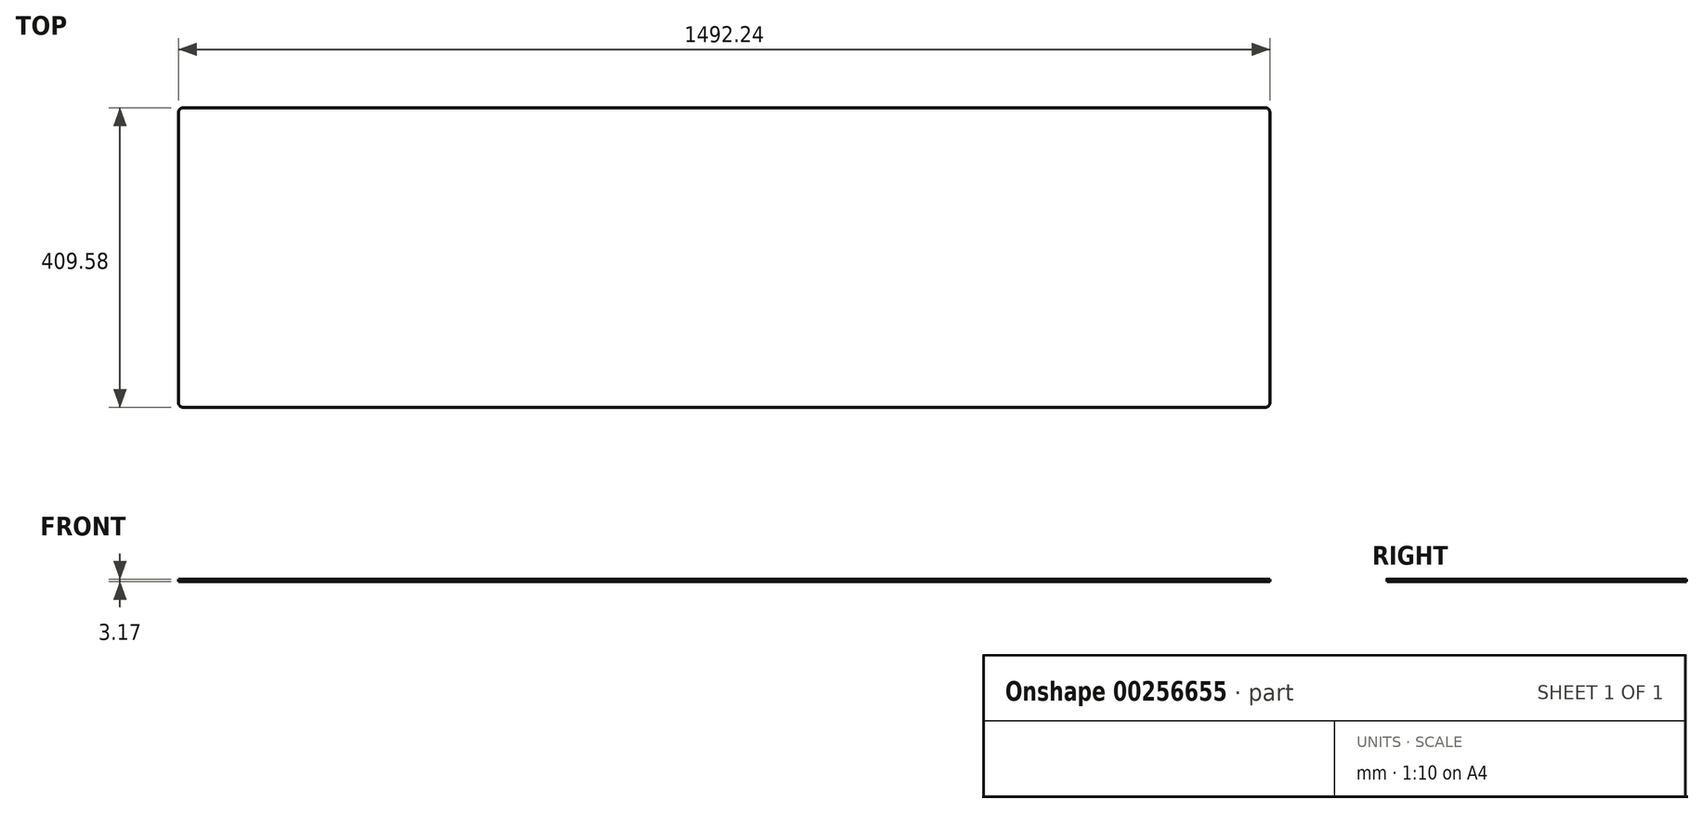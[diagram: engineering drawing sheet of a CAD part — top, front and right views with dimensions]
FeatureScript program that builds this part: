
annotation { "Feature Type Name" : "Feature", "Feature Type Description" : "" }
export const myFeature = defineFeature(function(context is Context, id is Id, definition is map)
    precondition{}
    {
        {
            var Q0;
            Q0=qCreatedBy(makeId("Top.planeOp"),FACE);
            var sketch = newSketch(context, id + "F0", { "sketchPlane" : qUnion([Q0])});
            skLineSegment(sketch, "E0.bottom", {"start": v(739.77, 204.79) * mm, "end": v(-739.78, 204.79) * mm});
            skLineSegment(sketch, "E0.top", {"start": v(739.78, -204.79) * mm, "end": v(-739.78, -204.79) * mm});
            skLineSegment(sketch, "E0.left", {"start": v(746.12, 198.44) * mm, "end": v(746.12, -198.44) * mm});
            skLineSegment(sketch, "E0.right", {"start": v(-746.12, 198.44) * mm, "end": v(-746.12, -198.44) * mm});
            skPoint(sketch, "E0.middle", {"position": v(0, 0) * mm});
            skPoint(sketch, "E1.visualSharp", {"position": v(746.12, -204.79) * mm});
            skArc(sketch, "E1.filletArc", {"start": v(739.78, -204.79) * mm, "mid": v(744.27, -202.93) * mm, "end": v(746.13, -198.44) * mm});
            skPoint(sketch, "E2.visualSharp", {"position": v(-746.12, -204.79) * mm});
            skArc(sketch, "E2.filletArc", {"start": v(-746.12, -198.44) * mm, "mid": v(-744.27, -202.93) * mm, "end": v(-739.78, -204.79) * mm});
            skPoint(sketch, "E3.visualSharp", {"position": v(746.12, 204.79) * mm});
            skArc(sketch, "E3.filletArc", {"start": v(746.12, 198.44) * mm, "mid": v(744.27, 202.93) * mm, "end": v(739.77, 204.79) * mm});
            skPoint(sketch, "E4.visualSharp", {"position": v(-746.12, 204.79) * mm});
            skArc(sketch, "E4.filletArc", {"start": v(-739.78, 204.79) * mm, "mid": v(-744.27, 202.93) * mm, "end": v(-746.13, 198.44) * mm});
            skSolve(sketch);
        }
        {
            var Q0;
            Q0=makeQuery(id+"F0.imprint","IMPRINT",FACE,{"disambiguationData":[TD([[makeQuery(id+"F0.imprint","IMPRINT",EDGE,{"derivedFrom":sQuery(id+"F0.wireOp",EDGE,"E0.bottom")}),1.0]])]});
            extrude(context, id + "F1", {"entities" : qUnion([Q0]), "depth" : 3.17 * mm});
        }
    });
